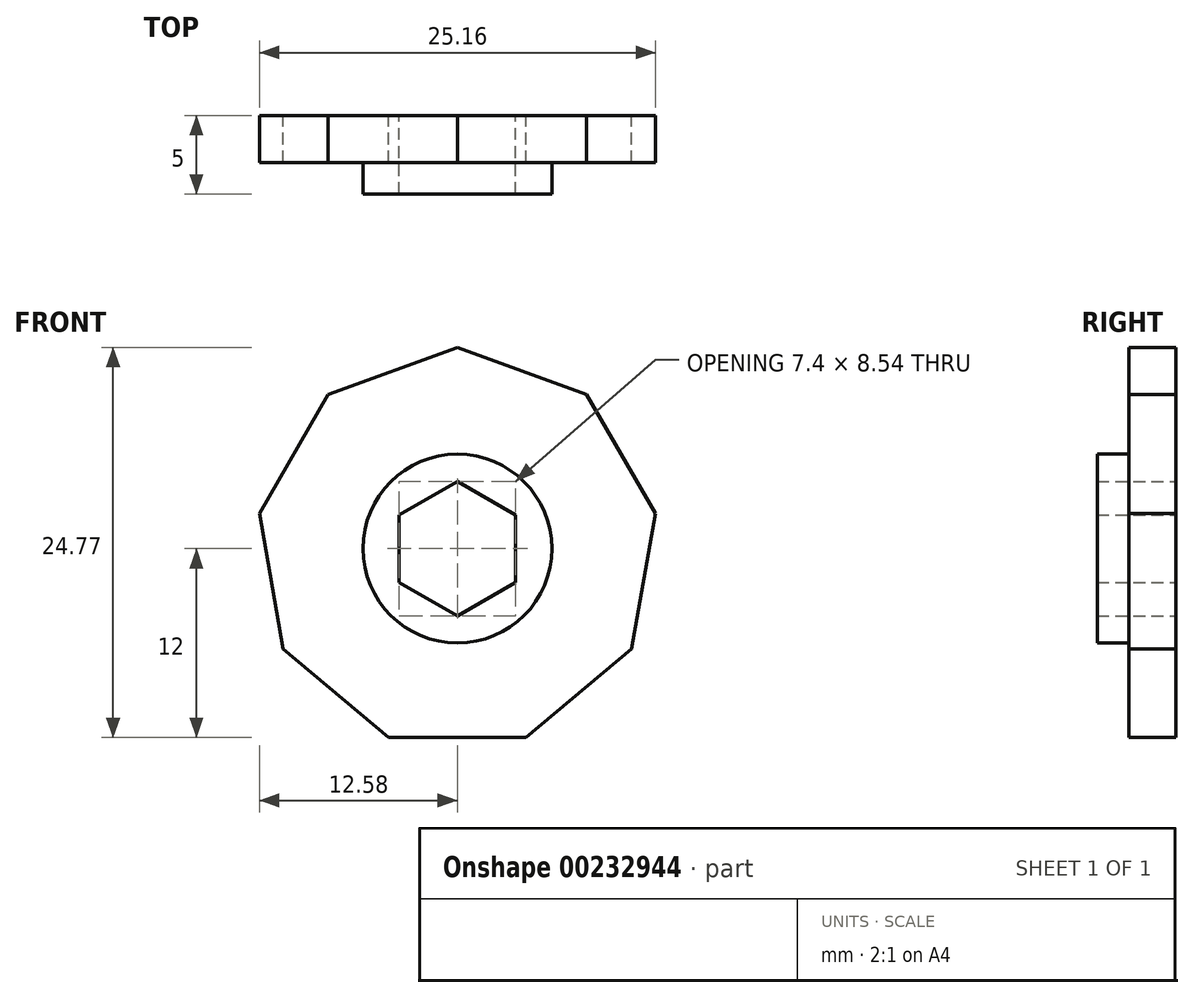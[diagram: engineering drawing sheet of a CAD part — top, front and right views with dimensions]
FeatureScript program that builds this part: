
annotation { "Feature Type Name" : "Feature", "Feature Type Description" : "" }
export const myFeature = defineFeature(function(context is Context, id is Id, definition is map)
    precondition{}
    {
        {
            var Q0;
            Q0=qCreatedBy(makeId("Front.planeOp"),FACE);
            var sketch = newSketch(context, id + "F0", { "sketchPlane" : qUnion([Q0])});
            skCircle(sketch, "E0.cCircle", {"center": v(0, 0) * mm, "radius": 3.7 * mm, "construction": true});
            skLineSegment(sketch, "E0.0", {"start": v(-3.7, -2.14) * mm, "end": v(-3.7, 2.14) * mm});
            skLineSegment(sketch, "E0.1", {"start": v(-3.7, 2.14) * mm, "end": v(0, 4.27) * mm});
            skLineSegment(sketch, "E0.2", {"start": v(0, 4.27) * mm, "end": v(3.7, 2.14) * mm});
            skLineSegment(sketch, "E0.3", {"start": v(3.7, 2.14) * mm, "end": v(3.7, -2.14) * mm});
            skLineSegment(sketch, "E0.4", {"start": v(3.7, -2.14) * mm, "end": v(0, -4.27) * mm});
            skLineSegment(sketch, "E0.5", {"start": v(0, -4.27) * mm, "end": v(-3.7, -2.14) * mm});
            skPoint(sketch, "E0.0.midPoint", {"position": v(-3.7, 0) * mm});
            skCircle(sketch, "E1", {"center": v(0, 0) * mm, "radius": 6 * mm});
            skCircle(sketch, "E2.cCircle", {"center": v(0, 0) * mm, "radius": 12 * mm, "construction": true});
            skLineSegment(sketch, "E2.0", {"start": v(4.37, -12) * mm, "end": v(-4.37, -12) * mm});
            skLineSegment(sketch, "E2.1", {"start": v(-4.37, -12) * mm, "end": v(-11.06, -6.39) * mm});
            skLineSegment(sketch, "E2.2", {"start": v(-11.06, -6.39) * mm, "end": v(-12.58, 2.22) * mm});
            skLineSegment(sketch, "E2.3", {"start": v(-12.58, 2.22) * mm, "end": v(-8.2, 9.78) * mm});
            skLineSegment(sketch, "E2.4", {"start": v(-8.2, 9.78) * mm, "end": v(0, 12.77) * mm});
            skLineSegment(sketch, "E2.5", {"start": v(0, 12.77) * mm, "end": v(8.2, 9.78) * mm});
            skLineSegment(sketch, "E2.6", {"start": v(8.2, 9.78) * mm, "end": v(12.58, 2.22) * mm});
            skLineSegment(sketch, "E2.7", {"start": v(12.58, 2.22) * mm, "end": v(11.06, -6.39) * mm});
            skLineSegment(sketch, "E2.8", {"start": v(11.06, -6.39) * mm, "end": v(4.37, -12) * mm});
            skPoint(sketch, "E2.0.midPoint", {"position": v(0, -12) * mm});
            skCircle(sketch, "E3", {"center": v(0, 0) * mm, "radius": 2.1 * mm});
            skSolve(sketch);
        }
        {
            var Q0;
            Q0=makeQuery(id+"F0.imprint","IMPRINT",FACE,{"disambiguationData":[TD([[makeQuery(id+"F0.imprint","IMPRINT",EDGE,{"derivedFrom":sQuery(id+"F0.wireOp",EDGE,"E1")}),-1.0]])]});
            extrude(context, id + "F1", {"entities" : qUnion([Q0]), "depth" : 3 * mm});
        }
        {
            var Q0;
            Q0=makeQuery(id+"F0.imprint","IMPRINT",FACE,{"disambiguationData":[TD([[makeQuery(id+"F0.imprint","IMPRINT",EDGE,{"derivedFrom":sQuery(id+"F0.wireOp",EDGE,"E0.0")}),1.0]])]});
            extrude(context, id + "F2", {"entities" : qUnion([Q0]), "operationType" : NewBodyOperationType.ADD, "depth" : 5 * mm});
        }
    });
